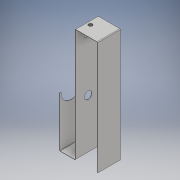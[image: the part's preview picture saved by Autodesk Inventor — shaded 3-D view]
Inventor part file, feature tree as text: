
AUTODESK INVENTOR PART (.ipt)
format: ipt  version: 2019 (Build 230136000, 136)  size: 176,640 bytes
history: native  units: mm
features: sheet_metal_op x13, sketch x9, other x5, hole x4
ambient origin geometry x8: Origin, YZ Plane, XZ Plane, XY Plane, X Axis, Y Axis, Z Axis, Center Point
bodies: Solid1 (feature_tree)
feature tree (31):
  sheet_metal_op  "Face1"
  sheet_metal_op  "Flange1"
  sheet_metal_op  "Flange2"
  sheet_metal_op  "Flange3"
  sheet_metal_op  "Flange4"
  hole  "Hole1"  [1 undecoded]
  hole  "Hole2"  [1 undecoded]
  hole  "Hole3"  [1 undecoded]
  hole  "Hole4"  [1 undecoded]
  sketch  "Sketch1"  dims[d0=180.0mm d1=36.0mm]
  other  "Plate1"
  sketch  "Sketch2"  dims[d2=0.5mm d3=0.5mm]
  other  "Plate2"
  sheet_metal_op  "Bend1"
  sheet_metal_op  "Corner1"
  sketch  "Sketch3"  dims[d4=0.25mm d5=1.0mm]
  other  "Plate3"
  sheet_metal_op  "Bend2"
  sheet_metal_op  "Corner2"
  sketch  "Sketch4"  dims[d6=0.5mm d7=36.0mm d8=90.0deg d9=0.5mm]
  other  "Plate4"
  sheet_metal_op  "Bend3"
  sheet_metal_op  "Corner3"
  sketch  "Sketch5"  dims[d10=2.0mm]
  other  "Plate5"
  sheet_metal_op  "Bend4"
  sheet_metal_op  "Corner4"
  sketch  "Sketch6"  dims[d11=0.5mm]
  sketch  "Sketch7"  dims[d12=0.5mm]
  sketch  "Sketch8"  dims[d13=0.5mm]
  sketch  "Sketch9"  dims[d14=0.25mm d15=1.0mm d16=0.5mm d17=180.0mm d18=90.0deg d19=0.5mm d20=2.0mm d21=0.5mm d22=0.5mm d23=0.5mm d24=0.25mm d25=1.0mm d26=0.5mm d27=25.0mm d28=90.0deg d29=0.5mm d30=2.0mm d31=0.5mm d32=0.5mm d33=0.5mm d34=0.25mm d35=1.0mm d36=0.5mm d37=80.0mm d38=90.0deg d39=0.5mm d40=2.0mm d41=0.5mm d42=0.5mm d43=33.0mm d44=6.0mm d45=4.0mm d46=2.0mm d47=90.0deg d48=33.0mm d49=20.594885mm d50=12.2mm d51=6.0mm d52=4.0mm d53=2.0mm d54=90.0deg d55=0.5mm d56=20.594885mm d57=6.0mm d58=6.0mm d59=4.0mm d60=2.0mm d61=90.0deg d62=0.75mm d63=20.594885mm d64=6.0mm d65=6.0mm d66=4.0mm d67=2.0mm d68=90.0deg d69=0.5mm d70=20.594885mm d71=0.75mm d72=20.594885mm d73=0.0625mm d74=0.75mm d75=0.375mm]
note: 4 required parameter values undecoded (feature->parameter linkage not recoverable at this tier; creation-order binding heuristic only, values carry confidence <= 0.55)
